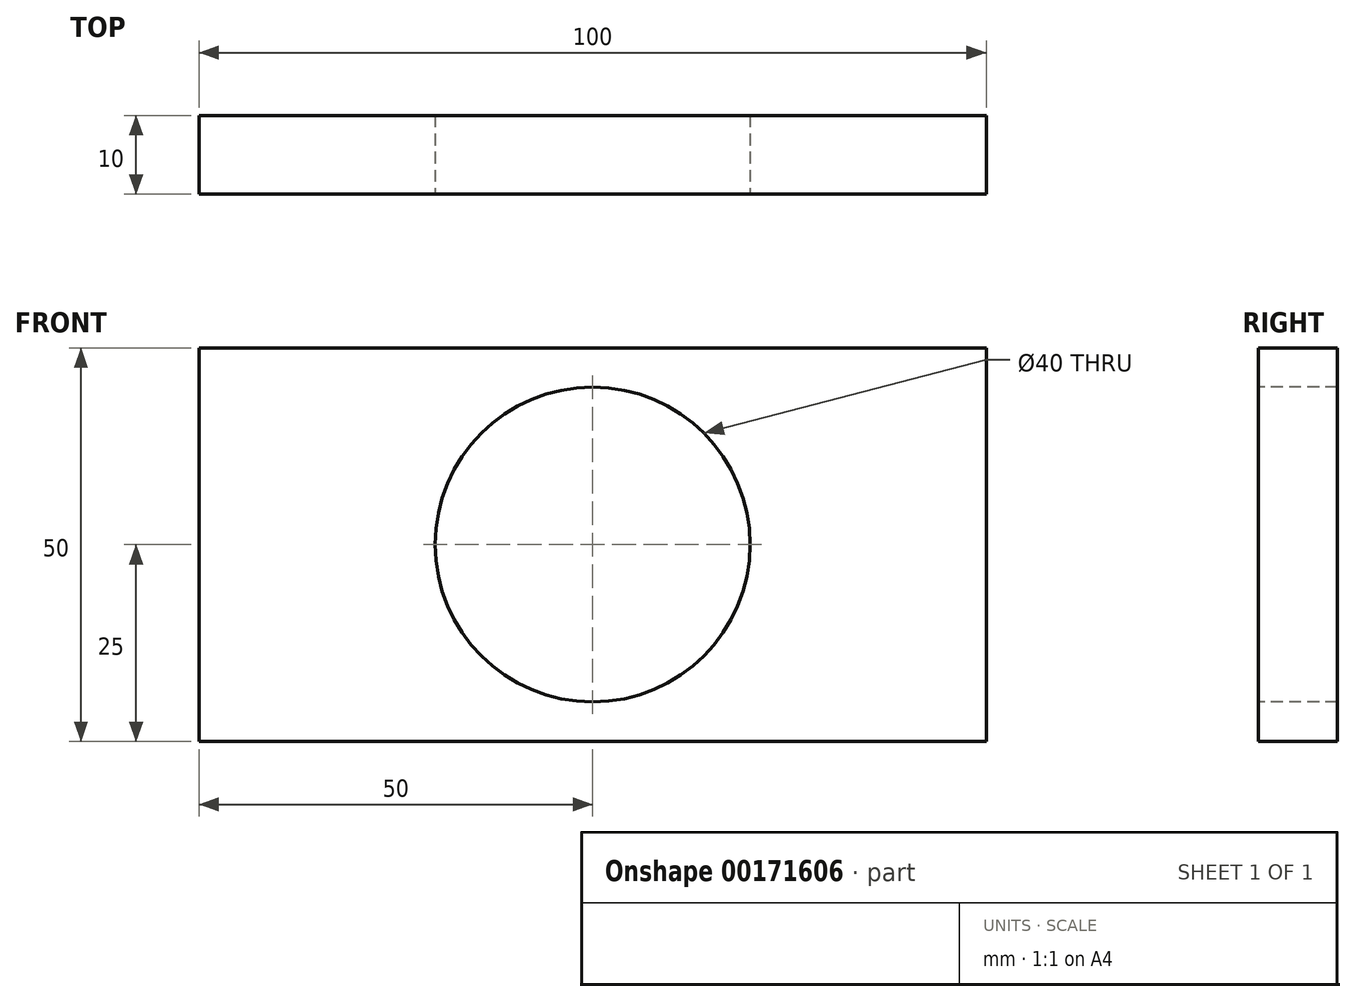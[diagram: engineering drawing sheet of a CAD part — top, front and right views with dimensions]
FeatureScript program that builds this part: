
annotation { "Feature Type Name" : "Feature", "Feature Type Description" : "" }
export const myFeature = defineFeature(function(context is Context, id is Id, definition is map)
    precondition{}
    {
        {
            var Q0;
            Q0=qCreatedBy(makeId("Front.planeOp"),FACE);
            var sketch = newSketch(context, id + "F0", { "sketchPlane" : qUnion([Q0])});
            skLineSegment(sketch, "E0.bottom", {"start": v(-50, 25) * mm, "end": v(50, 25) * mm});
            skLineSegment(sketch, "E0.top", {"start": v(-50, -25) * mm, "end": v(50, -25) * mm});
            skLineSegment(sketch, "E0.left", {"start": v(-50, 25) * mm, "end": v(-50, -25) * mm});
            skLineSegment(sketch, "E0.right", {"start": v(50, 25) * mm, "end": v(50, -25) * mm});
            skSolve(sketch);
        }
        {
            var Q0;
            Q0=makeQuery(id+"F0.imprint","IMPRINT",FACE,{"disambiguationData":[TD([[makeQuery(id+"F0.imprint","IMPRINT",EDGE,{"derivedFrom":sQuery(id+"F0.wireOp",EDGE,"E0.bottom")}),-1.0]])]});
            extrude(context, id + "F1", {"entities" : qUnion([Q0]), "oppositeDirection" : true, "depth" : 10 * mm});
        }
        {
            var Q0;
            Q0=makeQuery(id+"F1.opExtrude","CAP_FACE",FACE,{"disambiguationData":[OSD([sQuery(id+"F0.wireOp",EDGE,"E0.bottom"),sQuery(id+"F0.wireOp",EDGE,"E0.top"),sQuery(id+"F0.wireOp",EDGE,"E0.left"),sQuery(id+"F0.wireOp",EDGE,"E0.right")])],"isStart":true});
            var sketch = newSketch(context, id + "F2", { "sketchPlane" : qUnion([Q0])});
            skCircle(sketch, "E1", {"center": v(0, 0) * mm, "radius": 20 * mm});
            skSolve(sketch);
        }
        {
            var Q0;
            Q0=makeQuery(id+"F2.imprint","IMPRINT",FACE,{"disambiguationData":[TD([[makeQuery(id+"F2.imprint","IMPRINT",EDGE,{"derivedFrom":sQuery(id+"F2.wireOp",EDGE,"E1")}),1.0]])]});
            var Q1;
            Q1=sQuery(id+"F2.wireOp",EDGE,"E1");
            extrude(context, id + "F3", {"entities" : qUnion([Q0]), "operationType" : NewBodyOperationType.REMOVE, "surfaceEntities" : qUnion([Q1]), "oppositeDirection" : true, "depth" : 45 * mm});
        }
    });
